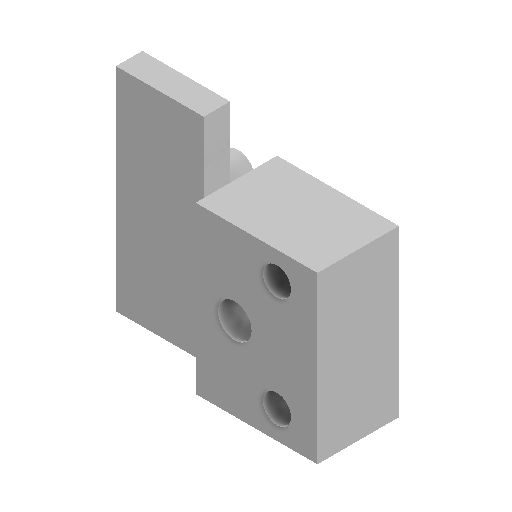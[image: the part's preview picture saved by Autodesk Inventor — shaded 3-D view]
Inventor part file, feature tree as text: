
AUTODESK INVENTOR PART (.ipt)
format: ipt  version: 2022 (Build 260153000, 153)  size: 157,184 bytes
history: native  units: mm
features: extrude x3, sketch x3, projected_geometry x2, other x2, reference x1
ambient origin geometry x8: Origin, YZ Plane, XZ Plane, XY Plane, X Axis, Y Axis, Z Axis, Center Point
bodies: Volumenkörper1 (feature_tree)
feature tree (11):
  extrude  "Extrusion1"  Depth=14.73mm
  extrude  "Extrusion2"  Depth=4.18mm
  extrude  "Extrusion3"  Depth=18.88mm
  sketch  "Skizze1"  dims[d1=3.6mm d2=14.73mm]
  reference  "Referenz1"
  sketch  "Skizze2"  dims[d3=10.83mm d4=4.18mm]
  projected_geometry  "Projizierte Kontur1"
  sketch  "Skizze3"  dims[d5=3.6mm d6=18.88mm d7=7.8mm d8=2.35mm d9=0.0mm d10=4.9mm d11=0.0mm d12=2.87mm d13=4.64mm d14=0.0mm]
  projected_geometry  "Projizierte Kontur2"
  other  "Assembly_Cube_Dichroic_Beamsplitter_multi_motorized_25x35_v3.iam"
  other  "00_Linear_Stepper_90mm:1"
